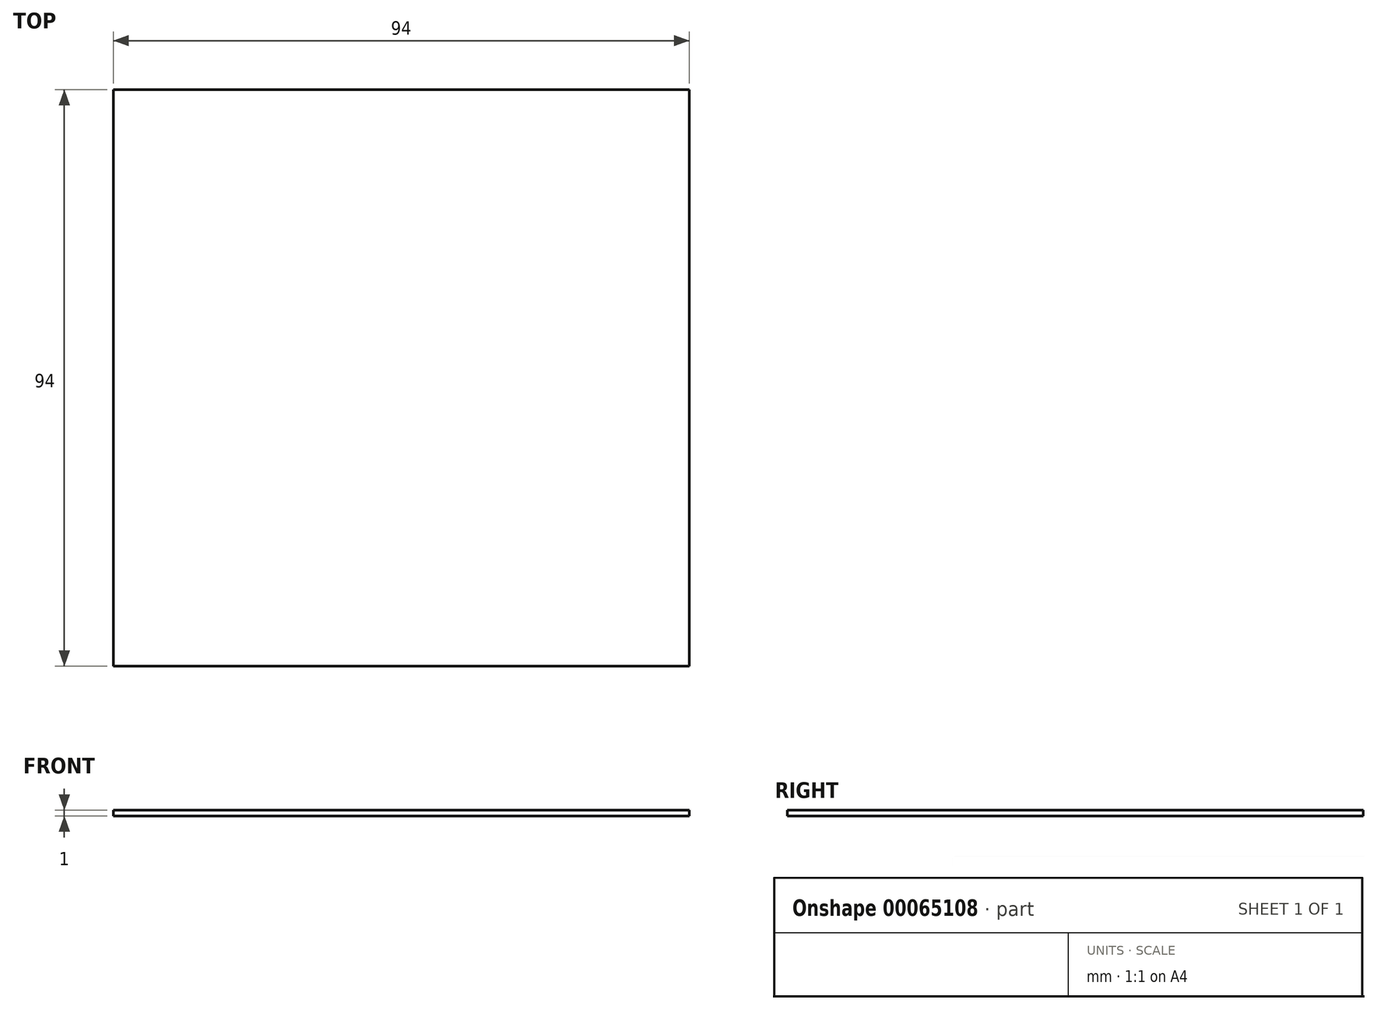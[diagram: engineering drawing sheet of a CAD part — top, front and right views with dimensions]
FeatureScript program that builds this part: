
annotation { "Feature Type Name" : "Feature", "Feature Type Description" : "" }
export const myFeature = defineFeature(function(context is Context, id is Id, definition is map)
    precondition{}
    {
        {
            var Q0;
            Q0=qCreatedBy(makeId("Top.planeOp"),FACE);
            var sketch = newSketch(context, id + "F0", { "sketchPlane" : qUnion([Q0])});
            skLineSegment(sketch, "E0.bottom", {"start": v(-47, 47) * mm, "end": v(47, 47) * mm});
            skLineSegment(sketch, "E0.top", {"start": v(-47, -47) * mm, "end": v(47, -47) * mm});
            skLineSegment(sketch, "E0.left", {"start": v(-47, 47) * mm, "end": v(-47, -47) * mm});
            skLineSegment(sketch, "E0.right", {"start": v(47, 47) * mm, "end": v(47, -47) * mm});
            skLineSegment(sketch, "E1", {"start": v(-47, 0) * mm, "end": v(47, 0) * mm, "construction": true});
            skLineSegment(sketch, "E2", {"start": v(0, 47) * mm, "end": v(0, -47) * mm, "construction": true});
            skSolve(sketch);
        }
        {
            var Q0;
            Q0 = qSketchRegion(id + "F0", true);
            extrude(context, id + "F1", {"entities" : qUnion([Q0]), "oppositeDirection" : true, "depth" : 1 * mm});
        }
    });
